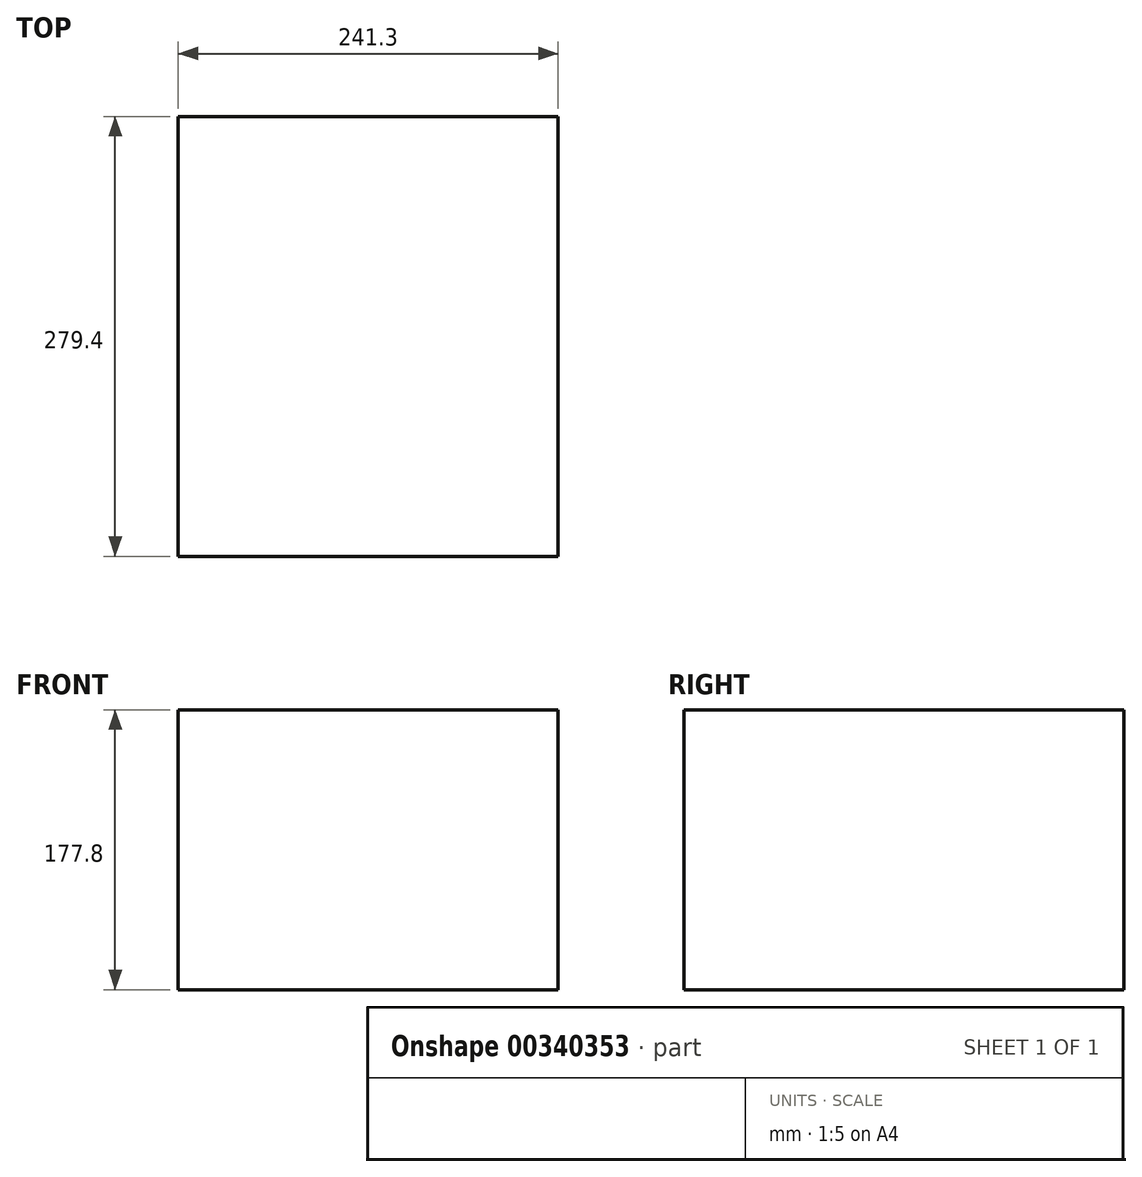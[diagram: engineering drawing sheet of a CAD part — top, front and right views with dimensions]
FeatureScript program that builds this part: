
annotation { "Feature Type Name" : "Feature", "Feature Type Description" : "" }
export const myFeature = defineFeature(function(context is Context, id is Id, definition is map)
    precondition{}
    {
        {
            var Q0;
            Q0=qCreatedBy(makeId("Front.planeOp"),FACE);
            var sketch = newSketch(context, id + "F0", { "sketchPlane" : qUnion([Q0])});
            skLineSegment(sketch, "E0.bottom", {"start": v(-225.34, 177.8) * mm, "end": v(15.96, 177.8) * mm});
            skLineSegment(sketch, "E0.top", {"start": v(-225.34, 0) * mm, "end": v(15.96, 0) * mm});
            skLineSegment(sketch, "E0.left", {"start": v(-225.34, 177.8) * mm, "end": v(-225.34, 0) * mm});
            skLineSegment(sketch, "E0.right", {"start": v(15.96, 177.8) * mm, "end": v(15.96, 0) * mm});
            skSolve(sketch);
        }
        {
            var Q0;
            Q0=makeQuery(id+"F0.imprint","IMPRINT",FACE,{"disambiguationData":[TD([[makeQuery(id+"F0.imprint","IMPRINT",EDGE,{"derivedFrom":sQuery(id+"F0.wireOp",EDGE,"E0.bottom")}),-1.0]])]});
            extrude(context, id + "F1", {"entities" : qUnion([Q0]), "depth" : 279.4 * mm});
        }
    });
